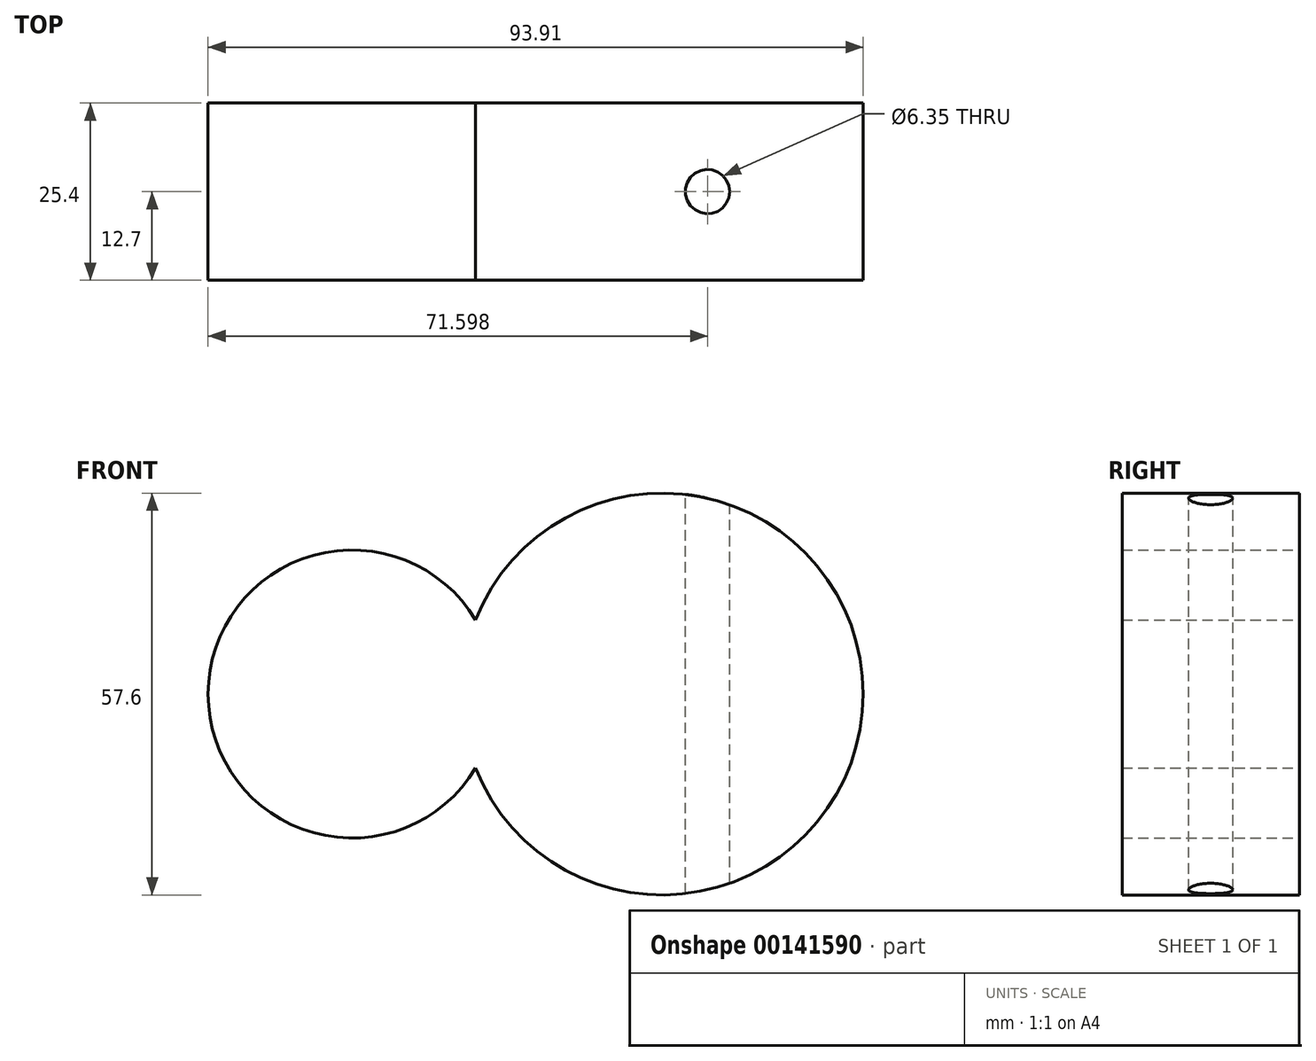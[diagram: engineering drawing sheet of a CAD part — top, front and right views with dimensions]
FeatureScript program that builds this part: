
annotation { "Feature Type Name" : "Feature", "Feature Type Description" : "" }
export const myFeature = defineFeature(function(context is Context, id is Id, definition is map)
    precondition{}
    {
        {
            var Q0;
            Q0=qCreatedBy(makeId("Front.planeOp"),FACE);
            var sketch = newSketch(context, id + "F0", { "sketchPlane" : qUnion([Q0])});
            skArc(sketch, "E0", {"start": v(-26.77, -10.62) * mm, "mid": v(28.8, 0) * mm, "end": v(-26.77, 10.62) * mm});
            skArc(sketch, "E1", {"start": v(-26.77, 10.62) * mm, "mid": v(-65.1, 0) * mm, "end": v(-26.77, -10.62) * mm});
            skSolve(sketch);
        }
        {
            var Q0;
            Q0=makeQuery(id+"F0.imprint","IMPRINT",FACE,{"disambiguationData":[TD([[makeQuery(id+"F0.imprint","IMPRINT",EDGE,{"derivedFrom":sQuery(id+"F0.wireOp",EDGE,"E0")}),1.0]])]});
            var Q1;
            Q1=sQuery(id+"F0.wireOp",EDGE,"E0");
            var Q2;
            Q2=sQuery(id+"F0.wireOp",EDGE,"E1");
            extrude(context, id + "F1", {"entities" : qUnion([Q0]), "surfaceEntities" : qUnion([Q1, Q2]), "endBound" : BoundingType.SYMMETRIC, "depth" : 25.4 * mm});
        }
        {
            var Q0;
            Q0=qCreatedBy(makeId("Top.planeOp"),FACE);
            cPlane(context, id + "F2", {"entities" : qUnion([Q0]), "cplaneType" : CPlaneType.OFFSET, "offset" : 50.8 * mm, "width" : 152.4 * mm, "height" : 152.4 * mm});
        }
        {
            var Q0;
            Q0=qCreatedBy(id+"F2.planeOp",FACE);
            var sketch = newSketch(context, id + "F3", { "sketchPlane" : qUnion([Q0])});
            skLineSegment(sketch, "E2", {"start": v(6.49, 12.7) * mm, "end": v(6.49, -12.7) * mm, "construction": true});
            skCircle(sketch, "E3", {"center": v(6.49, 0) * mm, "radius": 3.18 * mm});
            skSolve(sketch);
        }
        {
            var Q0;
            Q0 = qSketchRegion(id + "F3", true);
            extrude(context, id + "F4", {"entities" : qUnion([Q0]), "oppositeDirection" : true, "depth" : 116.85 * mm});
        }
        {
            var Q0;
            Q0=makeQuery(id+"F4.opExtrude","SWEPT_BODY",BODY,{"disambiguationData":[OSD([sQuery(id+"F3.wireOp",EDGE,"E3")])]});
            var Q1;
            Q1=makeQuery(id+"F1.opExtrude","SWEPT_BODY",BODY,{"disambiguationData":[OSD([sQuery(id+"F0.wireOp",EDGE,"E0"),sQuery(id+"F0.wireOp",EDGE,"E1")])]});
            booleanBodies(context, id + "F5", {"operationType" : BooleanOperationType.SUBTRACTION, "tools" : qUnion([Q0]), "targets" : qUnion([Q1])});
        }
    });
